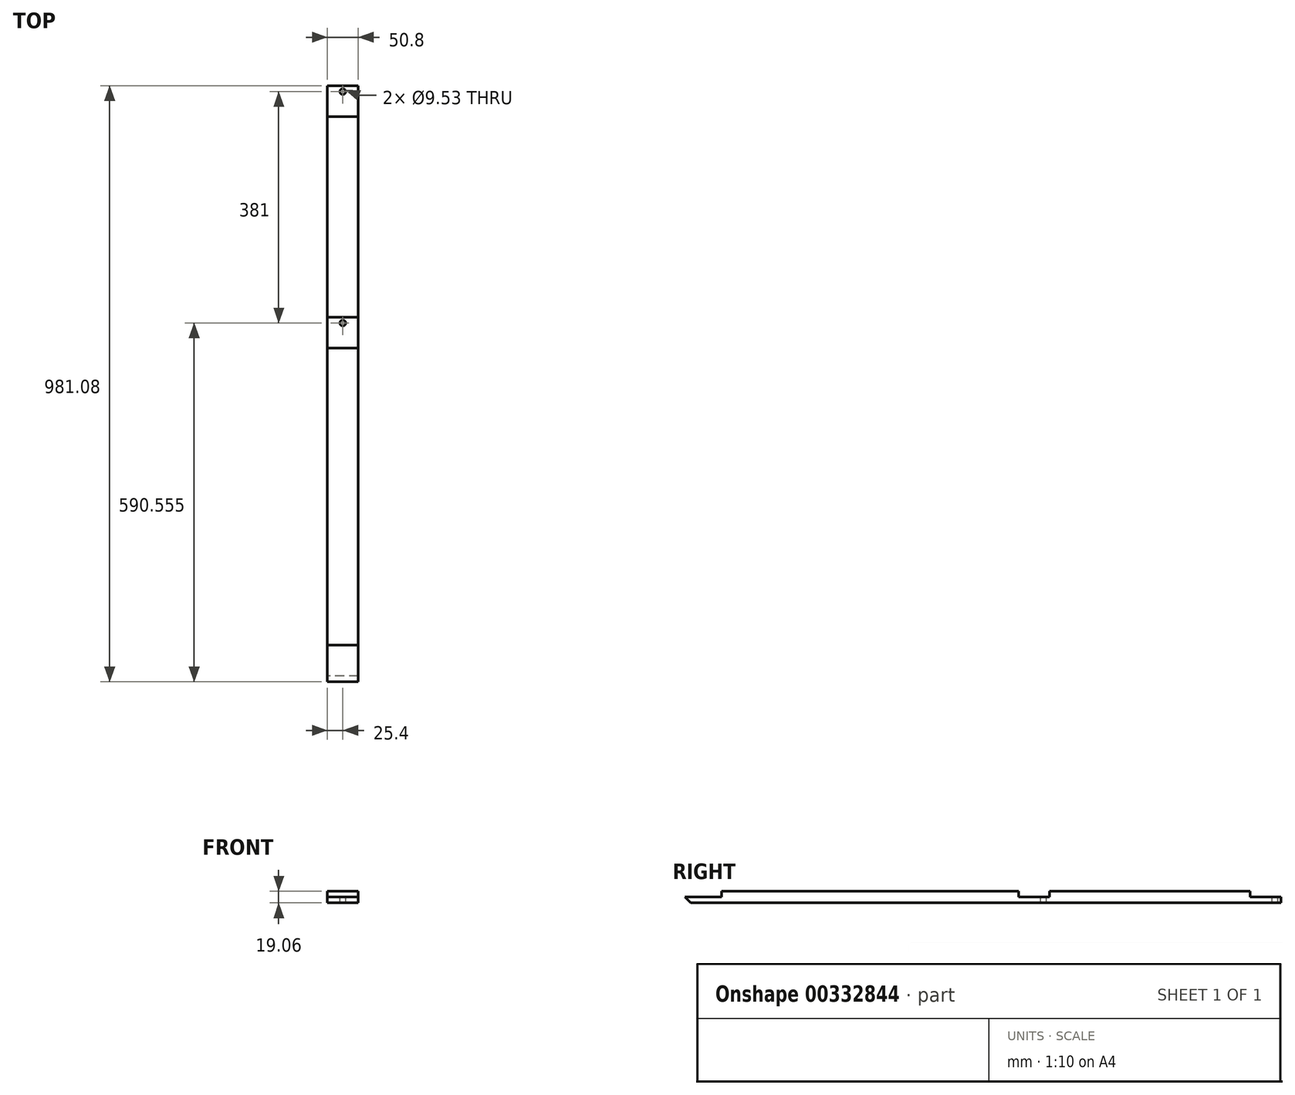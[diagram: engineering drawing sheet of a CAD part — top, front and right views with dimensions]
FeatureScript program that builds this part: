
annotation { "Feature Type Name" : "Feature", "Feature Type Description" : "" }
export const myFeature = defineFeature(function(context is Context, id is Id, definition is map)
    precondition{}
    {
        {
            var Q0;
            Q0=qCreatedBy(makeId("Right.planeOp"),FACE);
            var sketch = newSketch(context, id + "F0", { "sketchPlane" : qUnion([Q0])});
            skLineSegment(sketch, "E0.right", {"start": v(0, 9.52) * mm, "end": v(406.4, 9.53) * mm});
            skLineSegment(sketch, "E1", {"start": v(838.2, -9.52) * mm, "end": v(-33.3, -9.53) * mm});
            skLineSegment(sketch, "E2.top", {"start": v(787.4, 9.53) * mm, "end": v(787.4, 0) * mm});
            skLineSegment(sketch, "E2.right", {"start": v(838.2, 0) * mm, "end": v(787.4, 0) * mm});
            skPoint(sketch, "E3.orphan", {"position": v(787.4, 48.5) * mm});
            skLineSegment(sketch, "E4", {"start": v(0, 9.52) * mm, "end": v(-82.55, 9.52) * mm});
            skLineSegment(sketch, "E5", {"start": v(-142.88, 0) * mm, "end": v(-133.35, -9.53) * mm});
            skLineSegment(sketch, "E6", {"start": v(-33.3, -9.53) * mm, "end": v(-133.35, -9.53) * mm});
            skPoint(sketch, "E7.start.orphan", {"position": v(431.8, 9.53) * mm});
            skLineSegment(sketch, "E8", {"start": v(838.2, 0) * mm, "end": v(838.2, -9.52) * mm});
            skLineSegment(sketch, "E9.top", {"start": v(457.2, 0) * mm, "end": v(406.4, 0) * mm});
            skLineSegment(sketch, "E9.left", {"start": v(457.2, 9.53) * mm, "end": v(457.2, 0) * mm});
            skLineSegment(sketch, "E9.right", {"start": v(406.4, 9.53) * mm, "end": v(406.4, 0) * mm});
            skLineSegment(sketch, "E10.trimOffspring", {"start": v(457.2, 9.53) * mm, "end": v(787.4, 9.53) * mm});
            skLineSegment(sketch, "E11.top", {"start": v(-82.55, 0) * mm, "end": v(-142.88, 0) * mm});
            skLineSegment(sketch, "E11.left", {"start": v(-82.55, 9.53) * mm, "end": v(-82.55, 0) * mm});
            skLineSegment(sketch, "E12.left", {"start": v(-199.4, 74.43) * mm, "end": v(-199.4, 75.37) * mm});
            skLineSegment(sketch, "E12.right", {"start": v(-37.42, 74.43) * mm, "end": v(-37.42, 75.37) * mm});
            skPoint(sketch, "E13.orphan", {"position": v(-178.56, 0) * mm});
            skPoint(sketch, "E14.orphan", {"position": v(-152.4, 9.52) * mm});
            skSolve(sketch);
        }
        {
            var Q0;
            Q0=qSketchRegion(id+"F0",true);
            extrude(context, id + "F1", {"entities" : qUnion([Q0]), "endBound" : BoundingType.SYMMETRIC, "depth" : 50.8 * mm});
        }
        {
            var Q0;
            Q0=qCreatedBy(makeId("Top.planeOp"),FACE);
            var sketch = newSketch(context, id + "F2", { "sketchPlane" : qUnion([Q0])});
            skCircle(sketch, "E15", {"center": v(0, 828.68) * mm, "radius": 4.76 * mm});
            skCircle(sketch, "E16", {"center": v(0, 447.68) * mm, "radius": 4.76 * mm});
            skSolve(sketch);
        }
        {
            var Q0;
            Q0 = qSketchRegion(id + "F2", true);
            extrude(context, id + "F3", {"entities" : qUnion([Q0]), "operationType" : NewBodyOperationType.REMOVE, "oppositeDirection" : true, "depth" : 25.4 * mm});
        }
    });
